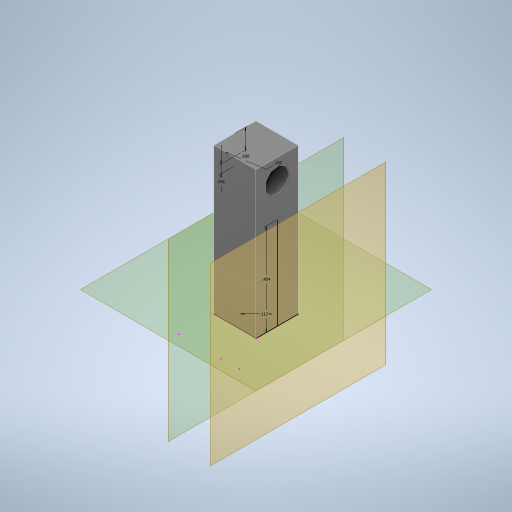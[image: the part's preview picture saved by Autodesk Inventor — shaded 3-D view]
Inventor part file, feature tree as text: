
AUTODESK INVENTOR PART (.ipt)
format: ipt  version: 2024 (Build 280153000, 153)  size: 375,808 bytes
history: native  units: in
note: dims shown in document units (in); Inventor stores cm internally (conversion verified against a paired STEP export)
features: plane x5, sketch x4, extrude x2, hole x1, thread x1
ambient origin geometry x8: Origin, YZ Plane, XZ Plane, XY Plane, X Axis, Y Axis, Z Axis, Center Point
bodies: Solid1 (feature_tree)
feature tree (13):
  plane  "Work Plane2"
  sketch  "Sketch1"  dims[d24=0.454in d25=0.0405in]
  plane  "Work Plane1"
  sketch  "Sketch2"  dims[d26=0.098in d27=0.12in]
  plane  "Work Plane3"
  plane  "Work Plane6"
  sketch  "Sketch5"  dims[d35=0.112in d36=0.72in d37=0.0in]
  plane  "Work Plane5"
  sketch  "Sketch6"  dims[d38=0.12in d39=0.75in d40=0.375in d41=0.25in d42=0.5635in d43=1.0in d44=0.8108in d45=0.46in d46=0.0in d47=0.46in d48=0.0in d17=1.0in d18=1.0in d19=1.0in d20=0.15in d21=0.25in d22=0.375in d23=0.5635in d28=0.375in]
  extrude  "Extrusion3"  Depth=0.0405in
  hole  "Hole4"  [1 undecoded]
  extrude  "Extrusion4"  Depth=0.72in TaperAngle=0.0deg
  thread  "Thread1"  [1 undecoded]
note: 2 required parameter values undecoded (feature->parameter linkage not recoverable at this tier; creation-order binding heuristic only, values carry confidence <= 0.55)
